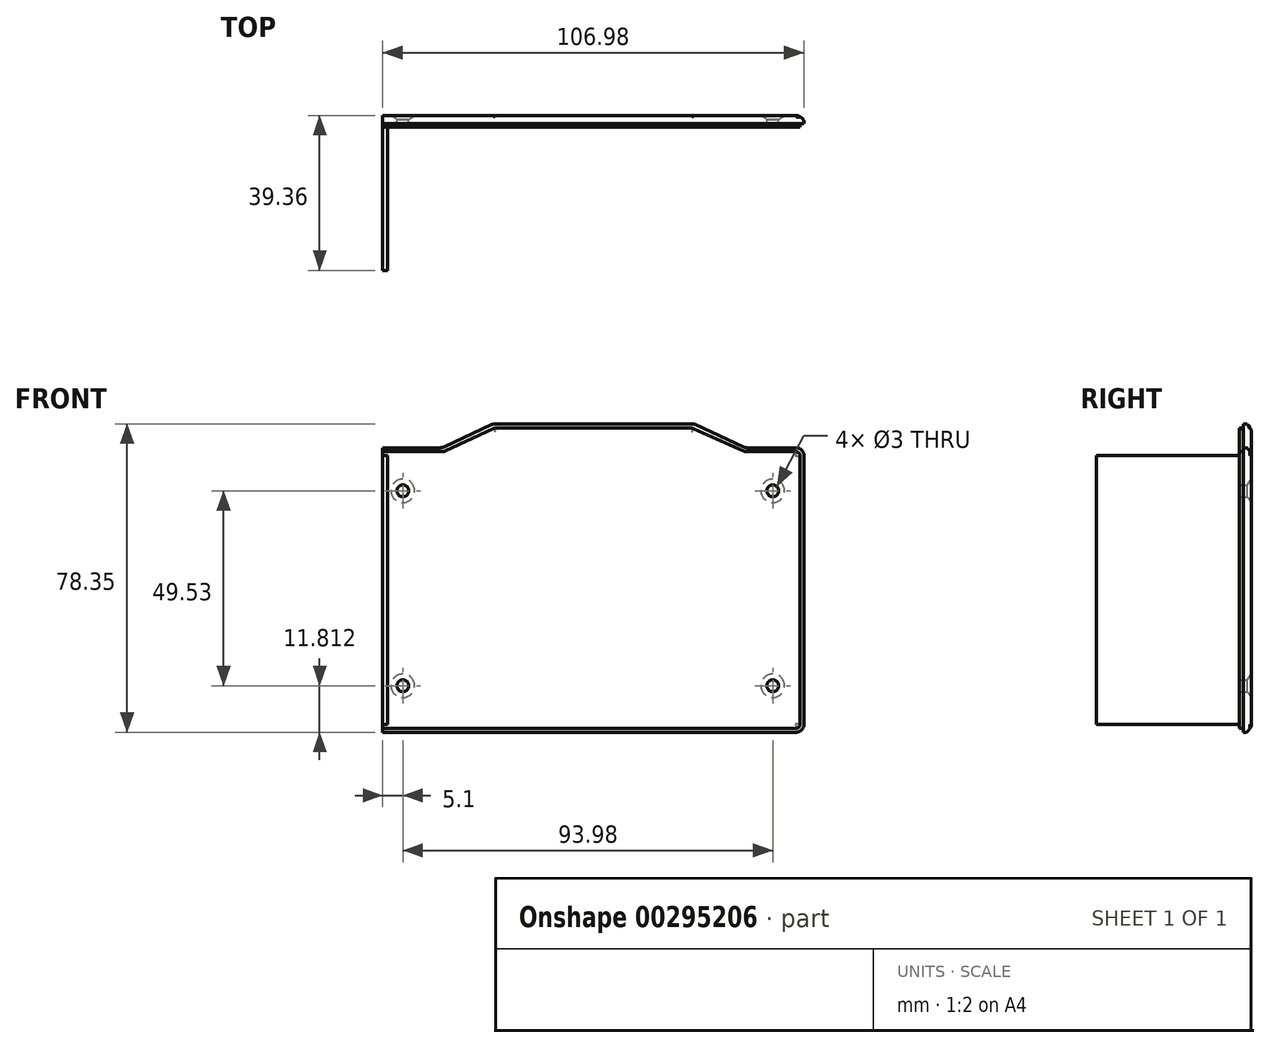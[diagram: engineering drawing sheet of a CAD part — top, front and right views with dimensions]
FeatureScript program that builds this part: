
annotation { "Feature Type Name" : "Feature", "Feature Type Description" : "" }
export const myFeature = defineFeature(function(context is Context, id is Id, definition is map)
    precondition{}
    {
        {
            var Q0;
            Q0=qCreatedBy(makeId("Front.planeOp"),FACE);
            var sketch = newSketch(context, id + "F0", { "sketchPlane" : qUnion([Q0])});
            skLineSegment(sketch, "E0", {"start": v(-119.96, -2) * mm, "end": v(-119.96, -70.29) * mm});
            skLineSegment(sketch, "E1", {"start": v(-117.96, -72.29) * mm, "end": v(-2, -72.29) * mm});
            skLineSegment(sketch, "E2", {"start": v(0, -70.29) * mm, "end": v(0, -2) * mm});
            skLineSegment(sketch, "E3", {"start": v(-79.29, 5.87) * mm, "end": v(-91.48, 0.19) * mm});
            skLineSegment(sketch, "E4", {"start": v(-92.33, 0) * mm, "end": v(-117.96, 0) * mm});
            skLineSegment(sketch, "E5", {"start": v(-2, 0) * mm, "end": v(-14.56, 0) * mm});
            skLineSegment(sketch, "E6", {"start": v(-15.4, 0.19) * mm, "end": v(-27.6, 5.87) * mm});
            skLineSegment(sketch, "E7", {"start": v(-28.44, 6.06) * mm, "end": v(-78.44, 6.06) * mm});
            skPoint(sketch, "E8.visualSharp", {"position": v(0, 0) * mm});
            skArc(sketch, "E8.filletArc", {"start": v(0, -2) * mm, "mid": v(-0.59, -0.59) * mm, "end": v(-2, 0) * mm});
            skPoint(sketch, "E9.visualSharp", {"position": v(-119.96, 0) * mm});
            skArc(sketch, "E9.filletArc", {"start": v(-117.96, 0) * mm, "mid": v(-119.37, -0.59) * mm, "end": v(-119.96, -2) * mm});
            skPoint(sketch, "E10.visualSharp", {"position": v(-119.96, -72.29) * mm});
            skArc(sketch, "E10.filletArc", {"start": v(-119.96, -70.29) * mm, "mid": v(-119.37, -71.7) * mm, "end": v(-117.96, -72.29) * mm});
            skPoint(sketch, "E11.visualSharp", {"position": v(0, -72.29) * mm});
            skArc(sketch, "E11.filletArc", {"start": v(-2, -72.29) * mm, "mid": v(-0.59, -71.7) * mm, "end": v(0, -70.29) * mm});
            skPoint(sketch, "E12.visualSharp", {"position": v(-15, 0) * mm});
            skArc(sketch, "E12.filletArc", {"start": v(-15.4, 0.19) * mm, "mid": v(-14.99, 0.05) * mm, "end": v(-14.56, 0) * mm});
            skPoint(sketch, "E13.visualSharp", {"position": v(-28, 6.06) * mm});
            skArc(sketch, "E13.filletArc", {"start": v(-27.6, 5.87) * mm, "mid": v(-28.01, 6.01) * mm, "end": v(-28.44, 6.06) * mm});
            skPoint(sketch, "E14.visualSharp", {"position": v(-78.89, 6.06) * mm});
            skArc(sketch, "E14.filletArc", {"start": v(-78.44, 6.06) * mm, "mid": v(-78.88, 6.01) * mm, "end": v(-79.29, 5.87) * mm});
            skPoint(sketch, "E15.visualSharp", {"position": v(-91.89, 0) * mm});
            skArc(sketch, "E15.filletArc", {"start": v(-92.33, 0) * mm, "mid": v(-91.9, 0.05) * mm, "end": v(-91.48, 0.19) * mm});
            skCircle(sketch, "E16", {"center": v(-101.88, -10.95) * mm, "radius": 1.5 * mm});
            skCircle(sketch, "E17", {"center": v(-101.88, -60.48) * mm, "radius": 1.5 * mm});
            skLineSegment(sketch, "E18", {"start": v(-101.88, -10.95) * mm, "end": v(3.2, -10.95) * mm, "construction": true});
            skCircle(sketch, "E19", {"center": v(-7.9, -60.48) * mm, "radius": 1.5 * mm});
            skCircle(sketch, "E20", {"center": v(-7.9, -10.95) * mm, "radius": 1.5 * mm});
            skSolve(sketch);
        }
        {
            var Q0;
            Q0=makeQuery(id+"F0.imprint","IMPRINT",FACE,{"disambiguationData":[TD([[makeQuery(id+"F0.imprint","IMPRINT",EDGE,{"derivedFrom":sQuery(id+"F0.wireOp",EDGE,"E0")}),1.0]])]});
            extrude(context, id + "F1", {"entities" : qUnion([Q0]), "depth" : 2 * mm});
        }
        {
            var Q0;
            Q0=makeQuery(id+"F1.opExtrude","CAP_FACE",FACE,{"disambiguationData":[OSD([sQuery(id+"F0.wireOp",EDGE,"E0"),sQuery(id+"F0.wireOp",EDGE,"E1"),sQuery(id+"F0.wireOp",EDGE,"E2"),sQuery(id+"F0.wireOp",EDGE,"E3"),sQuery(id+"F0.wireOp",EDGE,"E4"),sQuery(id+"F0.wireOp",EDGE,"E5"),sQuery(id+"F0.wireOp",EDGE,"E6"),sQuery(id+"F0.wireOp",EDGE,"E7")])],"isStart":true});
            chamfer(context, id + "F2", {"entities" : qUnion([Q0]), "chamferType" : ChamferType.TWO_OFFSETS, "width1" : 1.5 * mm, "oppositeDirection" : true, "width2" : 1 * mm, "tangentPropagation" : true});
        }
        {
            var Q0;
            {var subQ0=sQuery(id+"F0.wireOp",EDGE,"E7");Q0=makeQuery(id+"F2.opChamfer","BLEND_EDGE",EDGE,{"blendedFrom":[makeQuery(id+"F1.opExtrude","CAP_EDGE",EDGE,{"disambiguationData":[OSD([subQ0])],"isStart":true}),makeQuery(id+"F1.opExtrude","SWEPT_FACE",FACE,{"disambiguationData":[OSD([subQ0])]})],"blendedInto":[makeQuery(id+"F1.opExtrude","SWEPT_FACE",FACE,{"disambiguationData":[OSD([subQ0])]})]});}
            fillet(context, id + "F3", {"entities" : qUnion([Q0]), "radius" : 1 * mm, "tangentPropagation" : true, "allowEdgeOverflow" : false});
        }
        {
            var Q0;
            {var subQ0=sQuery(id+"F0.wireOp",EDGE,"E7");Q0=makeQuery(id+"F2.opChamfer","BLEND_EDGE",EDGE,{"blendedFrom":[makeQuery(id+"F1.opExtrude","CAP_EDGE",EDGE,{"disambiguationData":[OSD([subQ0])],"isStart":true}),makeQuery(id+"F1.opExtrude","CAP_FACE",FACE,{"disambiguationData":[OSD([sQuery(id+"F0.wireOp",EDGE,"E0"),sQuery(id+"F0.wireOp",EDGE,"E1"),sQuery(id+"F0.wireOp",EDGE,"E2"),sQuery(id+"F0.wireOp",EDGE,"E3"),sQuery(id+"F0.wireOp",EDGE,"E4"),sQuery(id+"F0.wireOp",EDGE,"E5"),sQuery(id+"F0.wireOp",EDGE,"E6"),subQ0])],"isStart":true})],"blendedInto":[makeQuery(id+"F1.opExtrude","CAP_FACE",FACE,{"disambiguationData":[OSD([sQuery(id+"F0.wireOp",EDGE,"E0"),sQuery(id+"F0.wireOp",EDGE,"E1"),sQuery(id+"F0.wireOp",EDGE,"E2"),sQuery(id+"F0.wireOp",EDGE,"E3"),sQuery(id+"F0.wireOp",EDGE,"E4"),sQuery(id+"F0.wireOp",EDGE,"E5"),sQuery(id+"F0.wireOp",EDGE,"E6"),subQ0])],"isStart":true})]});}
            fillet(context, id + "F4", {"entities" : qUnion([Q0]), "radius" : 2 * mm, "tangentPropagation" : true, "allowEdgeOverflow" : false});
        }
        {
            var Q0;
            Q0=makeQuery(id+"F1.opExtrude","CAP_FACE",FACE,{"disambiguationData":[OSD([sQuery(id+"F0.wireOp",EDGE,"E0"),sQuery(id+"F0.wireOp",EDGE,"E1"),sQuery(id+"F0.wireOp",EDGE,"E2"),sQuery(id+"F0.wireOp",EDGE,"E3"),sQuery(id+"F0.wireOp",EDGE,"E4"),sQuery(id+"F0.wireOp",EDGE,"E5"),sQuery(id+"F0.wireOp",EDGE,"E6"),sQuery(id+"F0.wireOp",EDGE,"E7"),sQuery(id+"F0.wireOp",EDGE,"E8.filletArc"),sQuery(id+"F0.wireOp",EDGE,"E9.filletArc"),sQuery(id+"F0.wireOp",EDGE,"E10.filletArc"),sQuery(id+"F0.wireOp",EDGE,"E11.filletArc"),sQuery(id+"F0.wireOp",EDGE,"E12.filletArc"),sQuery(id+"F0.wireOp",EDGE,"E13.filletArc"),sQuery(id+"F0.wireOp",EDGE,"E14.filletArc"),sQuery(id+"F0.wireOp",EDGE,"E15.filletArc"),sQuery(id+"F0.wireOp",EDGE,"E16"),sQuery(id+"F0.wireOp",EDGE,"E17"),sQuery(id+"F0.wireOp",EDGE,"E19"),sQuery(id+"F0.wireOp",EDGE,"E20")])],"isStart":false});
            var sketch = newSketch(context, id + "F5", { "sketchPlane" : qUnion([Q0])});
            skLineSegment(sketch, "E21.bottom", {"start": v(-121.96, 2) * mm, "end": v(-106.98, 2) * mm});
            skLineSegment(sketch, "E21.top", {"start": v(-121.96, -74.29) * mm, "end": v(-106.98, -74.29) * mm});
            skLineSegment(sketch, "E21.left", {"start": v(-121.96, 2) * mm, "end": v(-121.96, -74.29) * mm});
            skLineSegment(sketch, "E21.right", {"start": v(-106.98, 2) * mm, "end": v(-106.98, -74.29) * mm});
            skSolve(sketch);
        }
        {
            var Q0;
            {var subQ1=sQuery(id+"F5.wireOp",EDGE,"E21.bottom");Q0=makeQuery(id+"F5.imprint","IMPRINT",FACE,{"disambiguationData":[TD([[makeQuery(id+"F5.imprint","IMPRINT",EDGE,{"derivedFrom":subQ1}),-1.0]])]});}
            var Q1;
            Q1=makeQuery(id+"F5.imprint","IMPRINT",FACE,{"disambiguationData":[TD([[makeQuery(id+"F5.imprint","IMPRINT",EDGE,{"derivedFrom":makeQuery(id+"F1.opExtrude","CAP_EDGE",EDGE,{"disambiguationData":[OSD([sQuery(id+"F0.wireOp",EDGE,"E0")])],"isStart":false})}),1.0]])]});
            extrude(context, id + "F6", {"entities" : qUnion([Q0, Q1]), "operationType" : NewBodyOperationType.REMOVE, "oppositeDirection" : true, "depth" : 25 * mm});
        }
        {
            var Q0;
            Q0=makeQuery(id+"F1.opExtrude","CAP_FACE",FACE,{"disambiguationData":[OSD([sQuery(id+"F0.wireOp",EDGE,"E0"),sQuery(id+"F0.wireOp",EDGE,"E1"),sQuery(id+"F0.wireOp",EDGE,"E2"),sQuery(id+"F0.wireOp",EDGE,"E3"),sQuery(id+"F0.wireOp",EDGE,"E4"),sQuery(id+"F0.wireOp",EDGE,"E5"),sQuery(id+"F0.wireOp",EDGE,"E6"),sQuery(id+"F0.wireOp",EDGE,"E7"),sQuery(id+"F0.wireOp",EDGE,"E8.filletArc"),sQuery(id+"F0.wireOp",EDGE,"E9.filletArc"),sQuery(id+"F0.wireOp",EDGE,"E10.filletArc"),sQuery(id+"F0.wireOp",EDGE,"E11.filletArc"),sQuery(id+"F0.wireOp",EDGE,"E12.filletArc"),sQuery(id+"F0.wireOp",EDGE,"E13.filletArc"),sQuery(id+"F0.wireOp",EDGE,"E14.filletArc"),sQuery(id+"F0.wireOp",EDGE,"E15.filletArc"),sQuery(id+"F0.wireOp",EDGE,"E16"),sQuery(id+"F0.wireOp",EDGE,"E17"),sQuery(id+"F0.wireOp",EDGE,"E19"),sQuery(id+"F0.wireOp",EDGE,"E20")])],"isStart":false});
            var sketch = newSketch(context, id + "F7", { "sketchPlane" : qUnion([Q0])});
            skLineSegment(sketch, "E22.bottom", {"start": v(-106.98, -2) * mm, "end": v(-105.78, -2) * mm});
            skLineSegment(sketch, "E22.top", {"start": v(-106.98, -70.29) * mm, "end": v(-105.78, -70.29) * mm});
            skLineSegment(sketch, "E22.left", {"start": v(-106.98, -2) * mm, "end": v(-106.98, -70.29) * mm});
            skLineSegment(sketch, "E22.right", {"start": v(-105.78, -2) * mm, "end": v(-105.78, -70.29) * mm});
            skSolve(sketch);
        }
        {
            var Q0;
            Q0=makeQuery(id+"F7.imprint","IMPRINT",FACE,{"disambiguationData":[TD([[makeQuery(id+"F7.imprint","IMPRINT",EDGE,{"derivedFrom":sQuery(id+"F7.wireOp",EDGE,"E22.bottom")}),-1.0]])]});
            extrude(context, id + "F8", {"entities" : qUnion([Q0]), "operationType" : NewBodyOperationType.ADD, "depth" : 37.36 * mm});
        }
        {
            var Q0;
            Q0=makeQuery(id+"F1.opExtrude","CAP_FACE",FACE,{"disambiguationData":[OSD([sQuery(id+"F0.wireOp",EDGE,"E0"),sQuery(id+"F0.wireOp",EDGE,"E1"),sQuery(id+"F0.wireOp",EDGE,"E2"),sQuery(id+"F0.wireOp",EDGE,"E3"),sQuery(id+"F0.wireOp",EDGE,"E4"),sQuery(id+"F0.wireOp",EDGE,"E5"),sQuery(id+"F0.wireOp",EDGE,"E6"),sQuery(id+"F0.wireOp",EDGE,"E7"),sQuery(id+"F0.wireOp",EDGE,"E8.filletArc"),sQuery(id+"F0.wireOp",EDGE,"E9.filletArc"),sQuery(id+"F0.wireOp",EDGE,"E10.filletArc"),sQuery(id+"F0.wireOp",EDGE,"E11.filletArc"),sQuery(id+"F0.wireOp",EDGE,"E12.filletArc"),sQuery(id+"F0.wireOp",EDGE,"E13.filletArc"),sQuery(id+"F0.wireOp",EDGE,"E14.filletArc"),sQuery(id+"F0.wireOp",EDGE,"E15.filletArc"),sQuery(id+"F0.wireOp",EDGE,"E16"),sQuery(id+"F0.wireOp",EDGE,"E17"),sQuery(id+"F0.wireOp",EDGE,"E19"),sQuery(id+"F0.wireOp",EDGE,"E20")])],"isStart":false});
            var sketch = newSketch(context, id + "F9", { "sketchPlane" : qUnion([Q0])});
            skLineSegment(sketch, "E23", {"start": v(-91.88, -1) * mm, "end": v(-106.98, -1) * mm});
            skPoint(sketch, "E23.startSnap0", {"position": v(-91.9, 0.05) * mm});
            skPoint(sketch, "E24.endSnap0", {"position": v(-78.88, 6.01) * mm});
            skPoint(sketch, "E25.endSnap0", {"position": v(-28.01, 6.01) * mm});
            skPoint(sketch, "E26.endSnap0", {"position": v(-14.99, 0.05) * mm});
            skLineSegment(sketch, "E27", {"start": v(-14.56, -1) * mm, "end": v(-2, -1) * mm});
            skLineSegment(sketch, "E28", {"start": v(-1, -2) * mm, "end": v(-1, -70.29) * mm});
            skArc(sketch, "E29", {"start": v(-1, -2) * mm, "mid": v(-1.3, -1.3) * mm, "end": v(-2, -1) * mm});
            skLineSegment(sketch, "E30", {"start": v(-2, -71.29) * mm, "end": v(-106.98, -71.29) * mm});
            skArc(sketch, "E31", {"start": v(-2, -71.29) * mm, "mid": v(-1.3, -71) * mm, "end": v(-1, -70.29) * mm});
            skPoint(sketch, "E32.visualSharp", {"position": v(-14.99, -1) * mm});
            skPoint(sketch, "E33.visualSharp", {"position": v(-91.9, -1) * mm});
            skArc(sketch, "E33.filletArc", {"start": v(-91.88, -1) * mm, "mid": v(-91.5, -0.96) * mm, "end": v(-91.13, -0.85) * mm});
            skLineSegment(sketch, "E34", {"start": v(-91.13, -0.85) * mm, "end": v(-78.85, 4.87) * mm});
            skLineSegment(sketch, "E35", {"start": v(-78, 5.06) * mm, "end": v(-28.98, 5.06) * mm});
            skPoint(sketch, "E36.visualSharp", {"position": v(-28.44, 5.06) * mm});
            skArc(sketch, "E36.filletArc", {"start": v(-27.98, 4.8) * mm, "mid": v(-28.46, 5) * mm, "end": v(-28.98, 5.06) * mm});
            skPoint(sketch, "E37.visualSharp", {"position": v(-78.44, 5.06) * mm});
            skArc(sketch, "E37.filletArc", {"start": v(-78, 5.06) * mm, "mid": v(-78.43, 5.01) * mm, "end": v(-78.85, 4.87) * mm});
            skLineSegment(sketch, "E38", {"start": v(-27.98, 4.8) * mm, "end": v(-15.38, -0.83) * mm});
            skArc(sketch, "E39.filletArc", {"start": v(-15.38, -0.83) * mm, "mid": v(-14.98, -0.96) * mm, "end": v(-14.56, -1) * mm});
            skSolve(sketch);
        }
        {
            var Q0;
            {var subQ6=sQuery(id+"F9.wireOp",EDGE,"E23");Q0=makeQuery(id+"F9.imprint","IMPRINT",FACE,{"disambiguationData":[TD([[makeQuery(id+"F9.imprint","IMPRINT",EDGE,{"derivedFrom":subQ6}),1.0]])]});}
            extrude(context, id + "F10", {"entities" : qUnion([Q0]), "operationType" : NewBodyOperationType.ADD, "depth" : 1 * mm});
        }
    });
